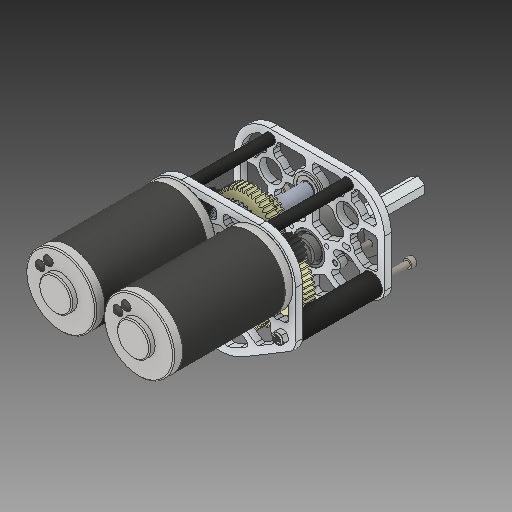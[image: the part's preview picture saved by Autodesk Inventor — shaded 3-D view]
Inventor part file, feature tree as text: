
AUTODESK INVENTOR PART (.ipt)
format: ipt  version: 2017 (Build 210142000, 142)  size: 10,811,392 bytes
history: native  units: in
note: dims shown in document units (in); Inventor stores cm internally (conversion verified against a paired STEP export)
features: other x74, sketch x1
ambient origin geometry x8: Origin, YZ Plane, XZ Plane, XY Plane, X Axis, Y Axis, Z Axis, Center Point
bodies: Solid1 (feature_tree), Solid2 (feature_tree), Solid3 (feature_tree), Solid4 (feature_tree), Solid5 (feature_tree), Solid6 (feature_tree), Solid7 (feature_tree), Solid8 (feature_tree), Solid9 (feature_tree), Solid10 (feature_tree), Solid11 (feature_tree), Solid12 (feature_tree), Solid13 (feature_tree), Solid14 (feature_tree), Solid15 (feature_tree), Solid16 (feature_tree), Solid17 (feature_tree), Solid18 (feature_tree), Solid19 (feature_tree), Solid20 (feature_tree), Solid21 (feature_tree), Solid22 (feature_tree), Solid23 (feature_tree), Solid24 (feature_tree), Solid25 (feature_tree), Solid26 (feature_tree), Solid27 (feature_tree), Solid28 (feature_tree), Solid29 (feature_tree), Solid30 (feature_tree), Solid31 (feature_tree), Solid32 (feature_tree), Solid33 (feature_tree), Solid34 (feature_tree), Solid35 (feature_tree), Solid36 (feature_tree), Solid37 (feature_tree), Solid38 (feature_tree), Solid39 (feature_tree), Solid40 (feature_tree), Solid41 (feature_tree), Solid42 (feature_tree), Solid43 (feature_tree), Solid44 (feature_tree), Solid45 (feature_tree), Solid46 (feature_tree), Solid47 (feature_tree), Solid48 (feature_tree), Solid49 (feature_tree), Solid50 (feature_tree), Solid51 (feature_tree), Solid52 (feature_tree), Solid53 (feature_tree), Solid54 (feature_tree), Solid55 (feature_tree), Solid56 (feature_tree), Solid57 (feature_tree), Solid58 (feature_tree), Solid59 (feature_tree), Solid60 (feature_tree), Solid61 (feature_tree), Solid62 (feature_tree), Solid63 (feature_tree), Solid64 (feature_tree), Solid65 (feature_tree), Solid66 (feature_tree), Solid67 (feature_tree), Solid68 (feature_tree), Solid69 (feature_tree), Solid70 (feature_tree), Solid71 (feature_tree), Solid72 (feature_tree)
feature tree (75):
  other  "WCP_DS_Gearbox.ipt"
  other  "Solid1::WCP_DS_Gearbox.ipt"
  other  "Solid2::WCP_DS_Gearbox.ipt"
  other  "Solid3::WCP_DS_Gearbox.ipt"
  other  "Solid4::WCP_DS_Gearbox.ipt"
  other  "Solid5::WCP_DS_Gearbox.ipt"
  other  "Solid6::WCP_DS_Gearbox.ipt"
  other  "Solid7::WCP_DS_Gearbox.ipt"
  other  "Solid8::WCP_DS_Gearbox.ipt"
  other  "Solid9::WCP_DS_Gearbox.ipt"
  other  "Solid10::WCP_DS_Gearbox.ipt"
  other  "Solid11::WCP_DS_Gearbox.ipt"
  other  "Solid12::WCP_DS_Gearbox.ipt"
  other  "Solid13::WCP_DS_Gearbox.ipt"
  other  "Solid14::WCP_DS_Gearbox.ipt"
  other  "Solid15::WCP_DS_Gearbox.ipt"
  other  "Solid16::WCP_DS_Gearbox.ipt"
  other  "Solid17::WCP_DS_Gearbox.ipt"
  other  "Solid18::WCP_DS_Gearbox.ipt"
  other  "Solid19::WCP_DS_Gearbox.ipt"
  other  "Solid20::WCP_DS_Gearbox.ipt"
  other  "Solid21::WCP_DS_Gearbox.ipt"
  other  "Solid22::WCP_DS_Gearbox.ipt"
  other  "Solid23::WCP_DS_Gearbox.ipt"
  other  "Solid24::WCP_DS_Gearbox.ipt"
  other  "Solid25::WCP_DS_Gearbox.ipt"
  other  "Solid26::WCP_DS_Gearbox.ipt"
  other  "Solid27::WCP_DS_Gearbox.ipt"
  other  "Solid28::WCP_DS_Gearbox.ipt"
  other  "Solid29::WCP_DS_Gearbox.ipt"
  other  "Solid30::WCP_DS_Gearbox.ipt"
  other  "Solid31::WCP_DS_Gearbox.ipt"
  other  "Solid32::WCP_DS_Gearbox.ipt"
  other  "Solid33::WCP_DS_Gearbox.ipt"
  other  "Solid34::WCP_DS_Gearbox.ipt"
  other  "Solid35::WCP_DS_Gearbox.ipt"
  other  "Solid36::WCP_DS_Gearbox.ipt"
  other  "Solid37::WCP_DS_Gearbox.ipt"
  other  "Solid38::WCP_DS_Gearbox.ipt"
  other  "Solid39::WCP_DS_Gearbox.ipt"
  other  "Solid40::WCP_DS_Gearbox.ipt"
  other  "Solid41::WCP_DS_Gearbox.ipt"
  other  "Solid42::WCP_DS_Gearbox.ipt"
  other  "Solid43::WCP_DS_Gearbox.ipt"
  other  "Solid44::WCP_DS_Gearbox.ipt"
  other  "Solid45::WCP_DS_Gearbox.ipt"
  other  "Solid46::WCP_DS_Gearbox.ipt"
  other  "Solid47::WCP_DS_Gearbox.ipt"
  other  "Solid48::WCP_DS_Gearbox.ipt"
  other  "Solid49::WCP_DS_Gearbox.ipt"
  other  "Solid50::WCP_DS_Gearbox.ipt"
  other  "Solid51::WCP_DS_Gearbox.ipt"
  other  "Solid52::WCP_DS_Gearbox.ipt"
  other  "Solid53::WCP_DS_Gearbox.ipt"
  other  "Solid54::WCP_DS_Gearbox.ipt"
  other  "Solid55::WCP_DS_Gearbox.ipt"
  other  "Solid56::WCP_DS_Gearbox.ipt"
  other  "Solid57::WCP_DS_Gearbox.ipt"
  other  "Solid58::WCP_DS_Gearbox.ipt"
  other  "Solid59::WCP_DS_Gearbox.ipt"
  other  "Solid60::WCP_DS_Gearbox.ipt"
  other  "Solid61::WCP_DS_Gearbox.ipt"
  other  "Solid62::WCP_DS_Gearbox.ipt"
  other  "Solid63::WCP_DS_Gearbox.ipt"
  other  "Solid64::WCP_DS_Gearbox.ipt"
  other  "Solid65::WCP_DS_Gearbox.ipt"
  other  "Solid66::WCP_DS_Gearbox.ipt"
  other  "Solid67::WCP_DS_Gearbox.ipt"
  other  "Solid68::WCP_DS_Gearbox.ipt"
  other  "Solid69::WCP_DS_Gearbox.ipt"
  other  "Solid70::WCP_DS_Gearbox.ipt"
  other  "Solid71::WCP_DS_Gearbox.ipt"
  other  "Solid72::WCP_DS_Gearbox.ipt"
  other  "TaggingFeature1"
  sketch  "Sketch1"  dims[d0=0.3937in]
